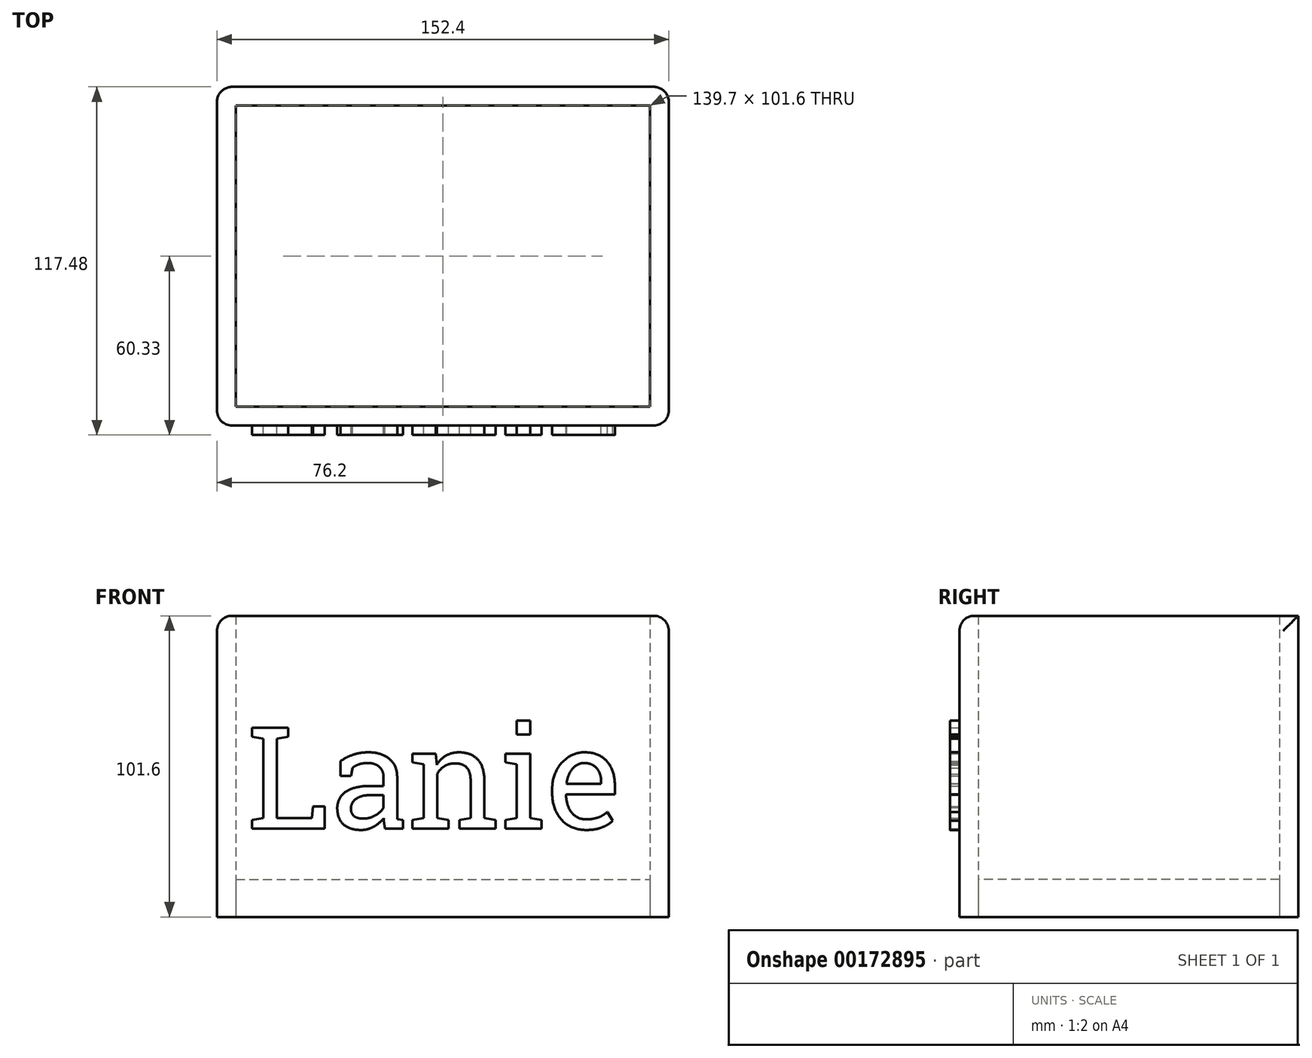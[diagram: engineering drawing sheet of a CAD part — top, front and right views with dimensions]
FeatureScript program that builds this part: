
annotation { "Feature Type Name" : "Feature", "Feature Type Description" : "" }
export const myFeature = defineFeature(function(context is Context, id is Id, definition is map)
    precondition{}
    {
        {
            var Q0;
            Q0=qCreatedBy(makeId("Top.planeOp"),FACE);
            var sketch = newSketch(context, id + "F0", { "sketchPlane" : qUnion([Q0])});
            skLineSegment(sketch, "E0.bottom", {"start": v(-76.2, 57.15) * mm, "end": v(76.2, 57.15) * mm});
            skLineSegment(sketch, "E0.top", {"start": v(-76.2, -57.15) * mm, "end": v(76.2, -57.15) * mm});
            skLineSegment(sketch, "E0.left", {"start": v(-76.2, 57.15) * mm, "end": v(-76.2, -57.15) * mm});
            skLineSegment(sketch, "E0.right", {"start": v(76.2, 57.15) * mm, "end": v(76.2, -57.15) * mm});
            skLineSegment(sketch, "E1.bottom", {"start": v(-69.85, 50.8) * mm, "end": v(69.85, 50.8) * mm});
            skLineSegment(sketch, "E1.top", {"start": v(-69.85, -50.8) * mm, "end": v(69.85, -50.8) * mm});
            skLineSegment(sketch, "E1.left", {"start": v(-69.85, 50.8) * mm, "end": v(-69.85, -50.8) * mm});
            skLineSegment(sketch, "E1.right", {"start": v(69.85, 50.8) * mm, "end": v(69.85, -50.8) * mm});
            skSolve(sketch);
        }
        {
            var Q0;
            Q0=makeQuery(id+"F0.imprint","IMPRINT",FACE,{"disambiguationData":[TD([[makeQuery(id+"F0.imprint","IMPRINT",EDGE,{"derivedFrom":sQuery(id+"F0.wireOp",EDGE,"E1.bottom")}),-1.0]])]});
            extrude(context, id + "F1", {"entities" : qUnion([Q0]), "depth" : 12.7 * mm});
        }
        {
            var Q0;
            Q0=makeQuery(id+"F0.imprint","IMPRINT",FACE,{"disambiguationData":[TD([[makeQuery(id+"F0.imprint","IMPRINT",EDGE,{"derivedFrom":sQuery(id+"F0.wireOp",EDGE,"E0.bottom")}),-1.0]])]});
            extrude(context, id + "F2", {"entities" : qUnion([Q0]), "depth" : 101.6 * mm});
        }
        {
            var Q0;
            Q0=makeQuery(id+"F2.opExtrude","CAP_EDGE",EDGE,{"disambiguationData":[OSD([sQuery(id+"F0.wireOp",EDGE,"E0.top")])],"isStart":false});
            var Q1;
            Q1=makeQuery(id+"F2.opExtrude","CAP_EDGE",EDGE,{"disambiguationData":[OSD([sQuery(id+"F0.wireOp",EDGE,"E0.right")])],"isStart":false});
            var Q2;
            Q2=makeQuery(id+"F2.opExtrude","SWEPT_EDGE",EDGE,{"disambiguationData":[OSD([sQuery(id+"F0.wireOp",EDGE,"E0.top"),sQuery(id+"F0.wireOp",EDGE,"E0.right")])]});
            var Q3;
            Q3=makeQuery(id+"F2.opExtrude","SWEPT_EDGE",EDGE,{"disambiguationData":[OSD([sQuery(id+"F0.wireOp",EDGE,"E0.bottom"),sQuery(id+"F0.wireOp",EDGE,"E0.right")])]});
            var Q4;
            Q4=makeQuery(id+"F2.opExtrude","CAP_EDGE",EDGE,{"disambiguationData":[OSD([sQuery(id+"F0.wireOp",EDGE,"E0.left")])],"isStart":false});
            var Q5;
            Q5=makeQuery(id+"F2.opExtrude","SWEPT_EDGE",EDGE,{"disambiguationData":[OSD([sQuery(id+"F0.wireOp",EDGE,"E0.top"),sQuery(id+"F0.wireOp",EDGE,"E0.left")])]});
            var Q6;
            Q6=makeQuery(id+"F2.opExtrude","SWEPT_EDGE",EDGE,{"disambiguationData":[OSD([sQuery(id+"F0.wireOp",EDGE,"E0.bottom"),sQuery(id+"F0.wireOp",EDGE,"E0.left")])]});
            fillet(context, id + "F3", {"entities" : qUnion([Q0, Q1, Q2, Q3, Q4, Q5, Q6]), "radius" : 5.08 * mm, "tangentPropagation" : true, "allowEdgeOverflow" : false});
        }
        {
            var Q0;
            Q0=makeQuery(id+"F2.opExtrude","SWEPT_FACE",FACE,{"disambiguationData":[OSD([sQuery(id+"F0.wireOp",EDGE,"E0.top")])]});
            var sketch = newSketch(context, id + "F4", { "sketchPlane" : qUnion([Q0])});
            skText(sketch, "E2", { "text": "Lanie", "fontName": "RobotoSlab-Regular.ttf"});
            const initialGuessF4  = {"E2": [-0.06604, 0.02982, 1, 0, 0.03442]};
            skSetInitialGuess(sketch, initialGuessF4);
            skSolve(sketch);
        }
        {
            var Q0;
            Q0 = qSketchRegion(id + "F4", true);
            extrude(context, id + "F5", {"entities" : qUnion([Q0]), "operationType" : NewBodyOperationType.ADD, "depth" : 3.17 * mm});
        }
    });
